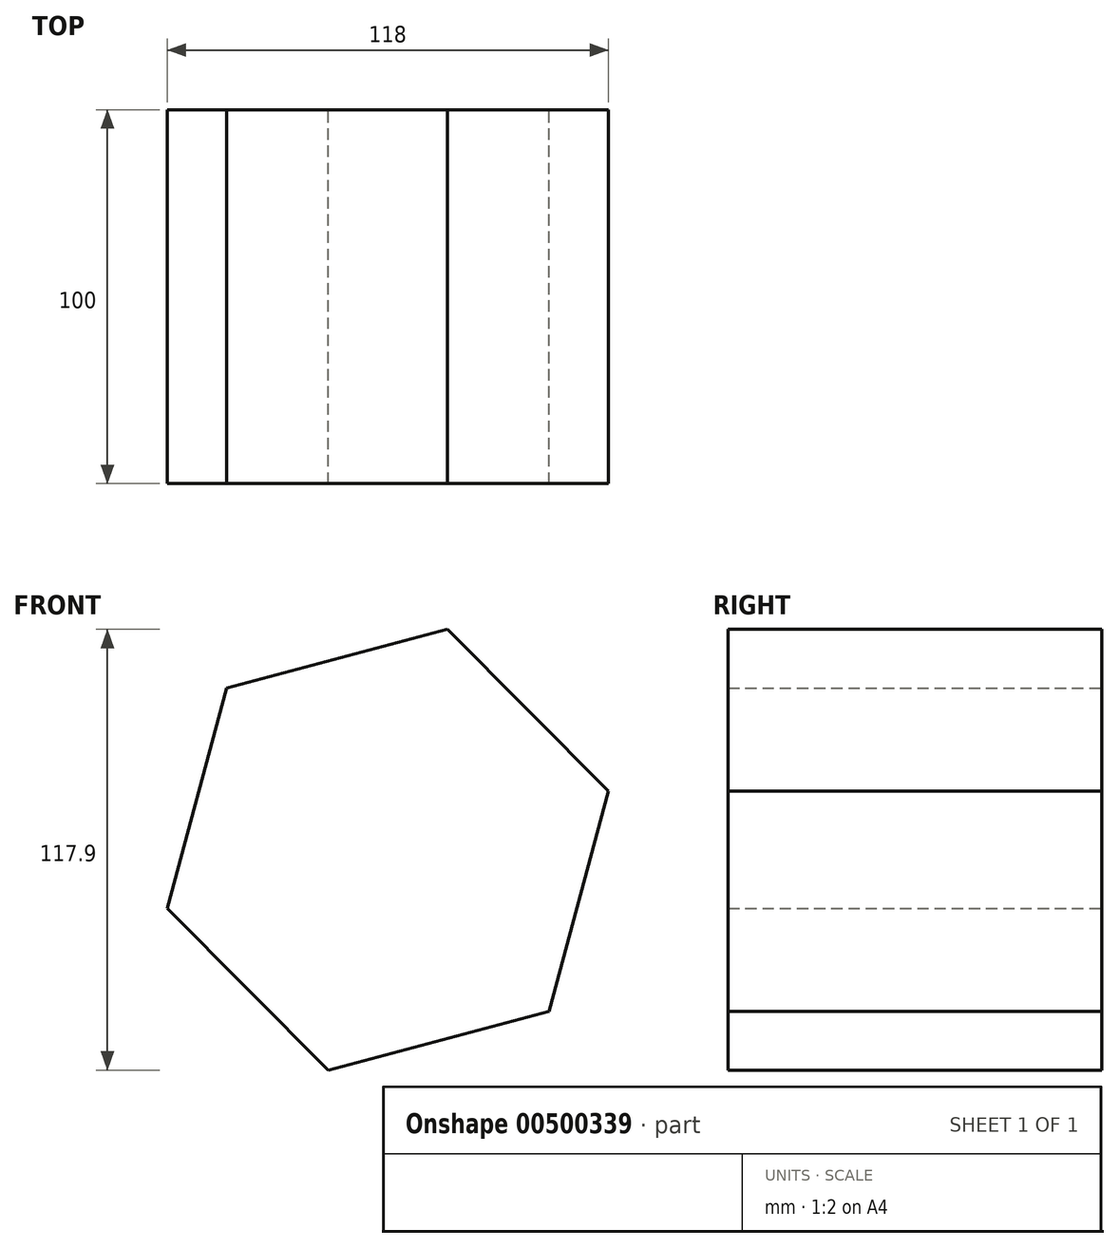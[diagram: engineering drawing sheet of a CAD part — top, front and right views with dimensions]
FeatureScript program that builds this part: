
annotation { "Feature Type Name" : "Feature", "Feature Type Description" : "" }
export const myFeature = defineFeature(function(context is Context, id is Id, definition is map)
    precondition{}
    {
        {
            var Q0;
            Q0=qCreatedBy(makeId("Front.planeOp"),FACE);
            var sketch = newSketch(context, id + "F0", { "sketchPlane" : qUnion([Q0])});
            skCircle(sketch, "E0.cCircle", {"center": v(0, 0) * mm, "radius": 61.06 * mm, "construction": true});
            skLineSegment(sketch, "E0.0", {"start": v(-15.9, -58.95) * mm, "end": v(-59, -15.7) * mm});
            skLineSegment(sketch, "E0.1", {"start": v(-59, -15.7) * mm, "end": v(-43.1, 43.24) * mm});
            skLineSegment(sketch, "E0.2", {"start": v(-43.1, 43.24) * mm, "end": v(15.9, 58.95) * mm});
            skLineSegment(sketch, "E0.3", {"start": v(15.9, 58.95) * mm, "end": v(59, 15.7) * mm});
            skLineSegment(sketch, "E0.4", {"start": v(59, 15.7) * mm, "end": v(43.1, -43.24) * mm});
            skLineSegment(sketch, "E0.5", {"start": v(43.1, -43.24) * mm, "end": v(-15.9, -58.95) * mm});
            skSolve(sketch);
        }
        {
            var Q0;
            Q0=makeQuery(id+"F0.imprint","IMPRINT",FACE,{"disambiguationData":[TD([[makeQuery(id+"F0.imprint","IMPRINT",EDGE,{"derivedFrom":sQuery(id+"F0.wireOp",EDGE,"E0.0")}),-1.0]])]});
            extrude(context, id + "F1", {"entities" : qUnion([Q0]), "depth" : 100 * mm});
        }
    });
